# Revit family: IKI
name_source: partatom
category: Furniture
revit_build: Autodesk Revit 2015 (Build: 20140606_1530(x64)
units: mm (PartAtom-declared; Revit-internal decimal feet)

## types (10) — shared parameters
Manufacturer = Isku Oy
Rocking chair armrest visibility = No
Type Comments = Available as antimicrobial
URL = www.isku.fi
Upholstery material = Fabric
Wooden parts = Birch

## per-type parameters (varying)
| type | Array high part | Array low part | Array number | High back | Low back | Seat Annotation lines visibility | Straight armrest visibility | Wooden armrest visibility | Wooden rocking chair armrest visibility | length |
| Matala keinu puisilla käsinojilla | No | No | 2 | No | Yes | No | No | No | Yes | 550 mm |
| Matala nojatuoli puukäsinojilla | No | No | 2 | No | Yes | No | No | Yes | No | 550 mm |
| Matala nojatuoli suoralla verhoilu käsinojalla | No | No | 2 | No | Yes | No | Yes | No | No | 550 mm |
| Korkea keinu puisilla käsinojilla | No | No | 2 | Yes | Yes | No | No | No | Yes | 550 mm |
| Korkea nojatuoli puukäsinojilla | No | No | 2 | Yes | Yes | No | No | Yes | No | 550 mm |
| Korkea nojatuoli suoralla verhoilukäsinojalla | No | No | 2 | Yes | Yes | No | Yes | No | No | 550 mm |
| 2h sohva korkea selkänoja suorilla käsinojilla | Yes | Yes | 2 | No | No | Yes | Yes | No | No | 1100 mm |
| 2h sohva matala selkänoja puukäsinojilla | No | Yes | 2 | No | No | Yes | No | Yes | No | 1100 mm |
| 3h sohva korkea selkänoja suorilla käsinojilla | Yes | Yes | 3 | No | No | Yes | Yes | No | No | 1650 mm  [stored 5.41339 ft] |
| 3h sohva matala selkänoja puukäsinojilla | No | Yes | 3 | No | No | Yes | No | Yes | No | 1650 mm  [stored 5.41339 ft] |

note: [stored X ft] marks values corroborated as IEEE doubles in the binary element streams (Revit-internal decimal feet)

## geometry (parser evidence)
native form markers: Sweep x20
no freeform markers — native parametric forms only
